# Revit family: 02-75-006 DN350 Increased Bore
name_source: partatom
category: Pipe Accessories
units: mm (PartAtom-declared; Revit-internal decimal feet)

## family parameters
Always vertical = Yes
Cut with Voids When Loaded = No
Part Type = Valve - Breaks Into
Round Connector Dimension = Use Diameter
Shared = No
Work Plane-Based = No

## types (2) — shared parameters
1 = 1 mm  [stored 0.00328084 ft]
5 = 5 mm  [stored 0.0164042 ft]
Body_FL_L = 282 mm
Body_FL_T = 55 mm  [stored 0.180446 ft]
Body_FL_W = 125 mm  [stored 0.410105 ft]
Body_H = 485 mm  [stored 1.59121 ft]
Body_L = 238 mm  [stored 0.78084 ft]
Body_R = 39 mm
Body_T = 13 mm
Body_W = 86 mm  [stored 0.282152 ft]
Bonnet_dim1 = 82 mm
Bonnet_dim2 = 49 mm
Bore = 175 mm  [stored 0.574147 ft]
DN = 350 mm  [stored 1.14829 ft]
DN350_PN10 = 02-450-75-504640003
DN350_PN16 = 02-450-75-514640003
Description_ = AVK GATE VALVE, FLANGED, PN10/16
F = 14 mm  [stored 0.0459318 ft]
F0 = 32 mm  [stored 0.104987 ft]
F1 = 15 mm  [stored 0.0492126 ft]
F11 = 37 mm  [stored 0.121391 ft]
F2 = 38 mm  [stored 0.124672 ft]
F22 = 55 mm  [stored 0.180446 ft]
FL_R = 69 mm
H = 1005 mm
H1 = 846 mm
H3 = 1265 mm
H3-H = 260 mm  [stored 0.853018 ft]
Increased_dim = 208 mm
L = 550 mm
L/2 = 275 mm
Logo height = 412 mm
Nut = 42 mm  [stored 0.137795 ft]
Raised_Dia = 215 mm
Raised_dis = 4 mm  [stored 0.0131234 ft]
Reduced_dim1 = 95 mm
Rib_H = 126 mm
Rib_L = 274 mm
Rib_T = 9 mm
Rib_W = 99 mm  [stored 0.324803 ft]
Search_table = 02-75-006 DN350 Increased Bore
Stand_Rib_W = 130 mm  [stored 0.426509 ft]
Stem_R = 41 mm
Stem_cap_H = 115 mm  [stored 0.377297 ft]
Stem_cap_dia = 75 mm  [stored 0.246063 ft]
URL_product_pages = https://www.avkvalves.com
disk_T = 109 mm
zero-valued in all types: Default Elevation

## per-type parameters (varying)
| type | FL_T |
| DN350_PN10 | 25 mm  [stored 0.082021 ft] |
| DN350_PN16 | 27 mm  [stored 0.0885827 ft] |

note: [stored X ft] marks values corroborated as IEEE doubles in the binary element streams (Revit-internal decimal feet)

## geometry (parser evidence)
native form markers: Sweep x2
no freeform markers — native parametric forms only
